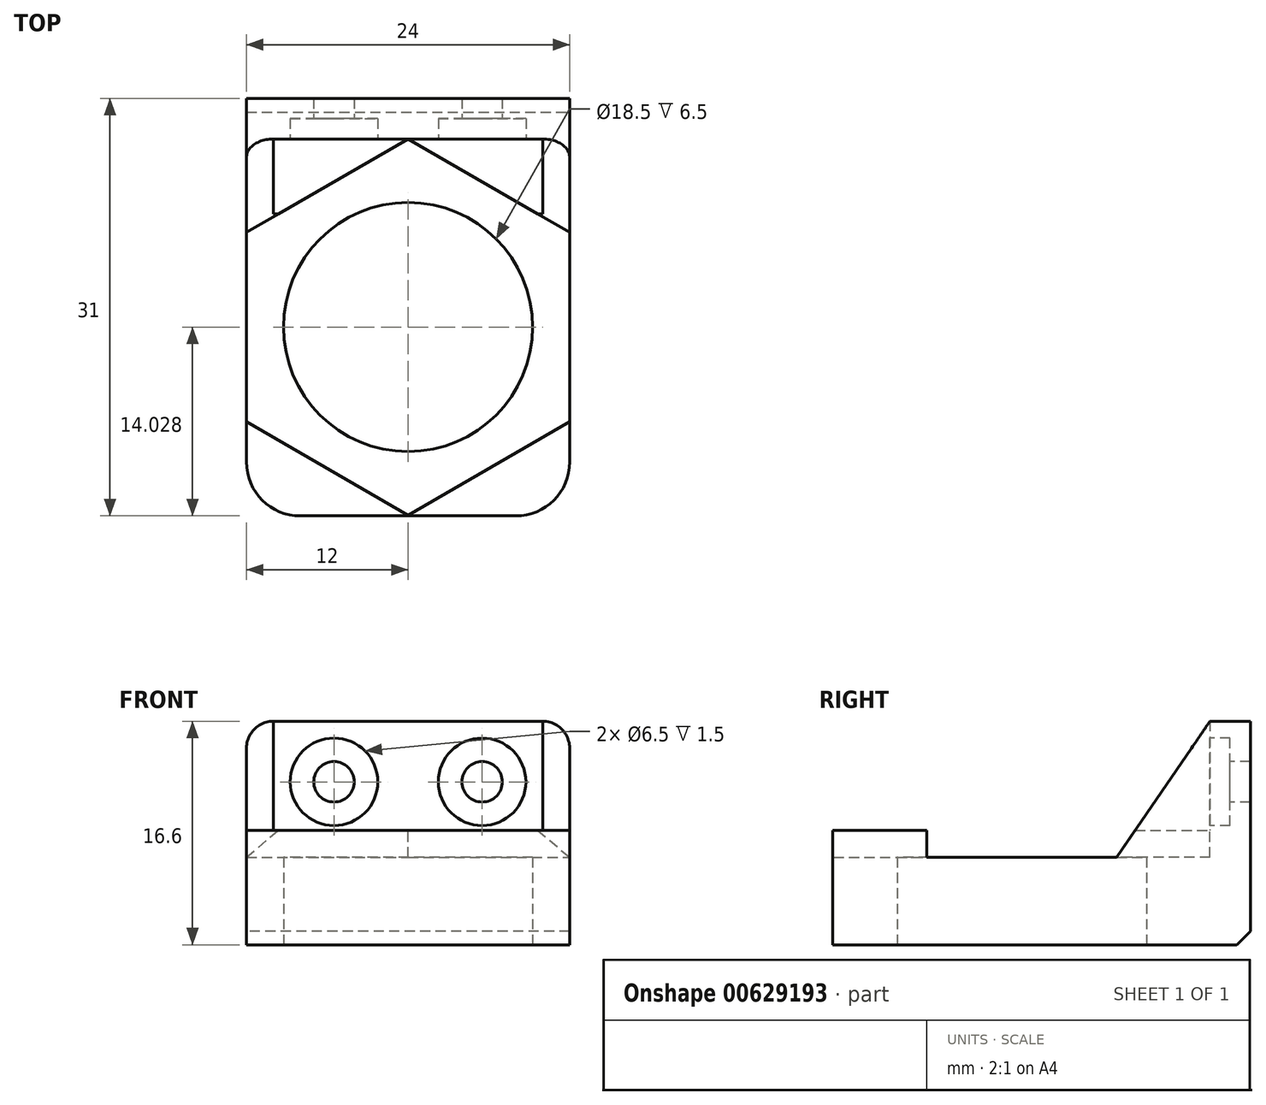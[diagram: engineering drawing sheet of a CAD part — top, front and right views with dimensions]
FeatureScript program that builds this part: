
annotation { "Feature Type Name" : "Feature", "Feature Type Description" : "" }
export const myFeature = defineFeature(function(context is Context, id is Id, definition is map)
    precondition{}
    {
        {
            var Q0;
            Q0=qCreatedBy(makeId("Front.planeOp"),FACE);
            var sketch = newSketch(context, id + "F0", { "sketchPlane" : qUnion([Q0])});
            skLineSegment(sketch, "E0.bottom", {"start": v(24, 11.6) * mm, "end": v(0, 11.6) * mm});
            skLineSegment(sketch, "E0.top", {"start": v(24, 0) * mm, "end": v(0, 0) * mm});
            skLineSegment(sketch, "E0.left", {"start": v(24, 11.6) * mm, "end": v(24, 0) * mm});
            skLineSegment(sketch, "E0.right", {"start": v(0, 11.6) * mm, "end": v(0, 0) * mm});
            skSolve(sketch);
        }
        {
            var Q0;
            Q0=makeQuery(id+"F0.imprint","IMPRINT",FACE,{"disambiguationData":[TD([[makeQuery(id+"F0.imprint","IMPRINT",EDGE,{"derivedFrom":sQuery(id+"F0.wireOp",EDGE,"E0.bottom")}),1.0]])]});
            extrude(context, id + "F1", {"entities" : qUnion([Q0]), "depth" : 3 * mm});
        }
        {
            var Q0;
            Q0=makeQuery(id+"F1.opExtrude","CAP_FACE",FACE,{"disambiguationData":[OSD([sQuery(id+"F0.wireOp",EDGE,"E0.bottom"),sQuery(id+"F0.wireOp",EDGE,"E0.top"),sQuery(id+"F0.wireOp",EDGE,"E0.left"),sQuery(id+"F0.wireOp",EDGE,"E0.right")])],"isStart":false});
            var sketch = newSketch(context, id + "F2", { "sketchPlane" : qUnion([Q0])});
            skLineSegment(sketch, "E1.bottom", {"start": v(0, 0) * mm, "end": v(24, 0) * mm});
            skLineSegment(sketch, "E1.top", {"start": v(0, 3.5) * mm, "end": v(24, 3.5) * mm});
            skLineSegment(sketch, "E1.left", {"start": v(0, 0) * mm, "end": v(0, 3.5) * mm});
            skLineSegment(sketch, "E1.right", {"start": v(24, 0) * mm, "end": v(24, 3.5) * mm});
            skLineSegment(sketch, "E2", {"start": v(0, 7.1) * mm, "end": v(24, 7.1) * mm, "construction": true});
            skLineSegment(sketch, "E3", {"start": v(17.5, 0) * mm, "end": v(17.5, 11.6) * mm, "construction": true});
            skLineSegment(sketch, "E4", {"start": v(6.5, 0) * mm, "end": v(6.5, 11.6) * mm, "construction": true});
            skPoint(sketch, "E5", {"position": v(6.5, 7.1) * mm});
            skPoint(sketch, "E6", {"position": v(17.5, 7.1) * mm});
            skCircle(sketch, "E7", {"center": v(6.5, 7.1) * mm, "radius": 2.35 * mm});
            skLineSegment(sketch, "E8", {"start": v(0, 5.8) * mm, "end": v(24, 5.8) * mm, "construction": true});
            skLineSegment(sketch, "E9", {"start": v(12, 11.6) * mm, "end": v(12, 0) * mm, "construction": true});
            skCircle(sketch, "E10.MirrorC", {"center": v(17.5, 7.1) * mm, "radius": 2.35 * mm});
            skLineSegment(sketch, "E11.bottom", {"start": v(0, 11.6) * mm, "end": v(2, 11.6) * mm});
            skLineSegment(sketch, "E11.top", {"start": v(0, 3.5) * mm, "end": v(2, 3.5) * mm});
            skLineSegment(sketch, "E11.left", {"start": v(0, 11.6) * mm, "end": v(0, 3.5) * mm});
            skLineSegment(sketch, "E11.right", {"start": v(2, 11.6) * mm, "end": v(2, 3.5) * mm});
            skLineSegment(sketch, "E12.MirrorCS", {"start": v(22, 11.6) * mm, "end": v(22, 3.5) * mm});
            skLineSegment(sketch, "E13.MirrorCS", {"start": v(24, 11.6) * mm, "end": v(22, 11.6) * mm});
            skLineSegment(sketch, "E14.MirrorCS", {"start": v(24, 11.6) * mm, "end": v(24, 3.5) * mm});
            skSolve(sketch);
        }
        {
            var Q0;
            Q0=sQuery(id+"F2.wireOp",VERTEX,"E5");
            var Q1;
            Q1=sQuery(id+"F2.wireOp",VERTEX,"E6");
            var Q2;
            Q2=sQuery(id+"F2.wireOp",VERTEX,"9b93672e-2990-476f-b0a9-77059a06add8");
            var Q3;
            Q3=sQuery(id+"F2.wireOp",VERTEX,"ac4e0633-efb0-4ba2-bce2-8fe4dab348f1");
            var Q4;
            Q4=makeQuery(id+"F1.opExtrude","SWEPT_BODY",BODY,{"disambiguationData":[OSD([sQuery(id+"F0.wireOp",EDGE,"E0.bottom"),sQuery(id+"F0.wireOp",EDGE,"E0.top"),sQuery(id+"F0.wireOp",EDGE,"E0.left"),sQuery(id+"F0.wireOp",EDGE,"E0.right")])]});
            hole(context, id + "F3", {"style" : HoleStyle.C_BORE, "endStyle" : HoleEndStyle.THROUGH, "holeDiameter" : 3 * mm, "cBoreDiameter" : 6.5 * mm, "cBoreDepth" : 1.5 * mm, "isTappedThrough" : true, "tappedDepth" : 12 * mm, "tapClearance" : 3, "locations" : qUnion([Q0, Q1, Q2, Q3]), "scope" : qUnion([Q4])});
        }
        {
            var Q0;
            Q0=makeQuery(id+"F2.imprint","IMPRINT",FACE,{"disambiguationData":[TD([[makeQuery(id+"F2.imprint","IMPRINT",EDGE,{"derivedFrom":sQuery(id+"F2.wireOp",EDGE,"E1.bottom")}),-1.0]])]});
            extrude(context, id + "F4", {"entities" : qUnion([Q0]), "operationType" : NewBodyOperationType.ADD, "depth" : 28 * mm});
        }
        {
            var Q0;
            {var subQ1=sQuery(id+"F2.wireOp",EDGE,"E1.top");Q0=makeQuery(id+"F2.imprint","IMPRINT",FACE,{"disambiguationData":[TD([[makeQuery(id+"F2.imprint","IMPRINT",EDGE,{"derivedFrom":subQ1}),1.0]])]});}
            var sketch = newSketch(context, id + "F5", { "sketchPlane" : qUnion([Q0])});
            skSolve(sketch);
        }
        {
            var Q0;
            Q0=makeQuery(id+"F4.opExtrude","SWEPT_FACE",FACE,{"disambiguationData":[OSD([sQuery(id+"F2.wireOp",EDGE,"E1.top")])]});
            var sketch = newSketch(context, id + "F6", { "sketchPlane" : qUnion([Q0])});
            skCircle(sketch, "E15.cCircle", {"center": v(12, -16.97) * mm, "radius": 12.1 * mm, "construction": true});
            skLineSegment(sketch, "E15.0", {"start": v(24.1, -9.99) * mm, "end": v(24.1, -23.96) * mm});
            skLineSegment(sketch, "E15.1", {"start": v(24.1, -23.96) * mm, "end": v(12, -30.94) * mm});
            skLineSegment(sketch, "E15.2", {"start": v(12, -30.94) * mm, "end": v(-0.1, -23.96) * mm});
            skLineSegment(sketch, "E15.3", {"start": v(-0.1, -23.96) * mm, "end": v(-0.1, -9.99) * mm});
            skLineSegment(sketch, "E15.4", {"start": v(-0.1, -9.99) * mm, "end": v(12, -3) * mm});
            skLineSegment(sketch, "E15.5", {"start": v(12, -3) * mm, "end": v(24.1, -9.99) * mm});
            skPoint(sketch, "E15.0.midPoint", {"position": v(24.1, -16.97) * mm});
            skLineSegment(sketch, "E16", {"start": v(12, -31) * mm, "end": v(12, -3) * mm, "construction": true});
            skSolve(sketch);
        }
        {
            var Q0;
            Q0=makeQuery(id+"F4.opExtrude","CAP_EDGE",EDGE,{"disambiguationData":[OSD([sQuery(id+"F2.wireOp",EDGE,"E1.right")])],"isStart":false});
            var Q1;
            Q1=makeQuery(id+"F5kRuORAZ8C9X0k_1.boolean.opBoolean","COPY",EDGE,{"derivedFrom":makeQuery(id+"F5kRuORAZ8C9X0k_1.opExtrude","SWEPT_EDGE",EDGE,{"disambiguationData":[OSD([sQuery(id+"F2.wireOp",EDGE,"E1.bottom"),sQuery(id+"F8.wireOp",EDGE,"GbdEAWLs-SJBU-rbzc-2olr-KBSKZh6psz5a")])]})});
            var Q2;
            Q2=makeQuery(id+"F5kRuORAZ8C9X0k_1.boolean.opBoolean","COPY",EDGE,{"derivedFrom":makeQuery(id+"F5kRuORAZ8C9X0k_1.opExtrude","SWEPT_EDGE",EDGE,{"disambiguationData":[OSD([sQuery(id+"F2.wireOp",EDGE,"E1.bottom"),sQuery(id+"F8.wireOp",EDGE,"kYlhJU9l-gKN5-24du-RjB6-uRuuNHYteBA4")])]})});
            var Q3;
            Q3=makeQuery(id+"F4.opExtrude","CAP_EDGE",EDGE,{"disambiguationData":[OSD([sQuery(id+"F2.wireOp",EDGE,"E1.left")])],"isStart":false});
            fillet(context, id + "F7", {"entities" : qUnion([Q0, Q1, Q2, Q3]), "radius" : 4 * mm, "tangentPropagation" : true, "allowEdgeOverflow" : false});
        }
        {
            var Q0;
            Q0=makeQuery(id+"F4.opExtrude","SWEPT_FACE",FACE,{"disambiguationData":[OSD([sQuery(id+"F2.wireOp",EDGE,"E1.bottom")])]});
            var sketch = newSketch(context, id + "F8", { "sketchPlane" : qUnion([Q0])});
            skLineSegment(sketch, "E17", {"start": v(12, 31.47) * mm, "end": v(12, 31) * mm, "construction": true});
            skCircle(sketch, "E18", {"center": v(12, 16.97) * mm, "radius": 9.25 * mm});
            skPoint(sketch, "E19", {"position": v(12, 0) * mm});
            skLineSegment(sketch, "E20", {"start": v(0, 17) * mm, "end": v(24, 17) * mm, "construction": true});
            skSolve(sketch);
        }
        {
            var Q0;
            Q0=makeQuery(id+"F8.imprint","IMPRINT",FACE,{"disambiguationData":[TD([[makeQuery(id+"F8.imprint","IMPRINT",EDGE,{"derivedFrom":sQuery(id+"F8.wireOp",EDGE,"E18")}),1.0]])]});
            extrude(context, id + "F9", {"entities" : qUnion([Q0]), "operationType" : NewBodyOperationType.REMOVE, "oppositeDirection" : true, "depth" : 25 * mm});
        }
        {
            var Q0;
            Q0=makeQuery(id+"F4.boolean.opBoolean","MERGE",FACE,{"derivedFrom":[makeQuery(id+"F1.opExtrude","SWEPT_FACE",FACE,{"disambiguationData":[OSD([sQuery(id+"F0.wireOp",EDGE,"E0.top")])]}),makeQuery(id+"F4.opExtrude","SWEPT_FACE",FACE,{"disambiguationData":[OSD([sQuery(id+"F2.wireOp",EDGE,"E1.bottom")])]})]});
            extrude(context, id + "F10", {"entities" : qUnion([Q0]), "operationType" : NewBodyOperationType.ADD, "depth" : 5 * mm});
        }
        {
            var Q0;
            {var subQ7=sQuery(id+"F6.wireOp",EDGE,"E15.2");var subQ8=sQuery(id+"F6.wireOp",EDGE,"E15.1");var subQ9=makeQuery(id+"F6.imprint","INTERSECT",VERTEX,{"derivedFrom":[subQ8,subQ7]});Q0=makeQuery(id+"F6.imprint","IMPRINT",FACE,{"disambiguationData":[TD([[makeQuery(id+"F6.imprint","IMPRINT",EDGE,{"disambiguationData":[TD([[subQ9,1.0]])],"derivedFrom":subQ8}),-1.0]])]});}
            extrude(context, id + "F11", {"entities" : qUnion([Q0]), "operationType" : NewBodyOperationType.REMOVE, "oppositeDirection" : true, "depth" : 2 * mm});
        }
        {
            var Q0;
            Q0=makeQuery(id+"F2.imprint","IMPRINT",FACE,{"disambiguationData":[TD([[makeQuery(id+"F2.imprint","IMPRINT",EDGE,{"derivedFrom":sQuery(id+"F2.wireOp",EDGE,"E11.bottom")}),1.0]])]});
            var Q1;
            Q1=makeQuery(id+"F11.boolean.opBoolean","COPY",FACE,{"derivedFrom":makeQuery(id+"F11.opExtrude","SWEPT_FACE",FACE,{"disambiguationData":[OSD([sQuery(id+"F6.wireOp",EDGE,"E15.4")])]})});
            var Q2;
            Q2=makeQuery(id+"F1.opExtrude","SWEPT_BODY",BODY,{"disambiguationData":[OSD([sQuery(id+"F0.wireOp",EDGE,"E0.bottom"),sQuery(id+"F0.wireOp",EDGE,"E0.top"),sQuery(id+"F0.wireOp",EDGE,"E0.left"),sQuery(id+"F0.wireOp",EDGE,"E0.right")])]});
            var Q3;
            Q3=sQuery(id+"F6.wireOp",VERTEX,"E15.4.start");
            extrude(context, id + "F12", {"entities" : qUnion([Q0]), "operationType" : NewBodyOperationType.ADD, "endBound" : BoundingType.UP_TO_SURFACE, "endBoundEntityFace" : qUnion([Q1]), "endBoundEntityBody" : qUnion([Q2]), "endBoundEntityVertex" : qUnion([Q3]), "depth" : 25 * mm});
        }
        {
            var Q0;
            {var subQ2=sQuery(id+"F2.wireOp",EDGE,"E12.MirrorCS");Q0=makeQuery(id+"F5.imprint","IMPRINT",FACE,{"disambiguationData":[TD([[makeQuery(id+"F5.imprint","IMPRINT",EDGE,{"derivedFrom":makeQuery(id+"F2.imprint","IMPRINT",EDGE,{"derivedFrom":subQ2})}),1.0]])]});}
            var Q1;
            Q1=makeQuery(id+"F11.boolean.opBoolean","COPY",FACE,{"derivedFrom":makeQuery(id+"F11.opExtrude","SWEPT_FACE",FACE,{"disambiguationData":[OSD([sQuery(id+"F6.wireOp",EDGE,"E15.5")])]})});
            extrude(context, id + "F13", {"entities" : qUnion([Q0]), "operationType" : NewBodyOperationType.ADD, "endBound" : BoundingType.UP_TO_SURFACE, "endBoundEntityFace" : qUnion([Q1]), "depth" : 25 * mm});
        }
        {
            var Q0;
            Q0=makeQuery(id+"F10.opExtrude","CAP_EDGE",EDGE,{"disambiguationData":[OSD([sQuery(id+"F0.wireOp",EDGE,"E0.top")])],"isStart":false});
            chamfer(context, id + "F14", {"entities" : qUnion([Q0]), "width" : 1 * mm, "tangentPropagation" : true});
        }
        {
            var Q0;
            Q0=makeQuery(id+"F1.opExtrude","SWEPT_EDGE",EDGE,{"disambiguationData":[OSD([sQuery(id+"F0.wireOp",EDGE,"E0.bottom"),sQuery(id+"F0.wireOp",EDGE,"E0.left")])]});
            var Q1;
            Q1=makeQuery(id+"F1.opExtrude","SWEPT_EDGE",EDGE,{"disambiguationData":[OSD([sQuery(id+"F0.wireOp",EDGE,"E0.bottom"),sQuery(id+"F0.wireOp",EDGE,"E0.right")])]});
            fillet(context, id + "F15", {"entities" : qUnion([Q0, Q1]), "radius" : 2 * mm, "tangentPropagation" : true, "allowEdgeOverflow" : false});
        }
        {
            var Q0;
            {var subQ0=sQuery(id+"F2.wireOp",EDGE,"E1.right");var subQ1=sQuery(id+"F0.wireOp",EDGE,"E0.left");Q0=makeQuery(id+"F13.boolean.opBoolean","MERGE",FACE,{"derivedFrom":[makeQuery(id+"F10.boolean.opBoolean","MERGE",FACE,{"derivedFrom":[makeQuery(id+"F4.boolean.opBoolean","MERGE",FACE,{"derivedFrom":[makeQuery(id+"F1.opExtrude","SWEPT_FACE",FACE,{"disambiguationData":[OSD([subQ1])]}),makeQuery(id+"F4.opExtrude","SWEPT_FACE",FACE,{"disambiguationData":[OSD([subQ0])]})]}),makeQuery(id+"F10.opExtrude","SWEPT_FACE",FACE,{"disambiguationData":[OSD([sQuery(id+"F0.wireOp",EDGE,"E0.top"),subQ1,sQuery(id+"F2.wireOp",EDGE,"E1.bottom"),subQ0])]})]}),makeQuery(id+"F13.opExtrude","SWEPT_FACE",FACE,{"disambiguationData":[OSD([sQuery(id+"F2.wireOp",EDGE,"E14.MirrorCS")])]})]});}
            var sketch = newSketch(context, id + "F16", { "sketchPlane" : qUnion([Q0])});
            skLineSegment(sketch, "E21", {"start": v(-9.93, 1.5) * mm, "end": v(-3, 11.6) * mm});
            skLineSegment(sketch, "E22", {"start": v(-3, 11.6) * mm, "end": v(-9.93, 11.6) * mm});
            skLineSegment(sketch, "E23", {"start": v(-9.93, 11.6) * mm, "end": v(-9.93, 1.5) * mm});
            skSolve(sketch);
        }
        {
            var Q0;
            Q0 = qSketchRegion(id + "F16", true);
            extrude(context, id + "F17", {"entities" : qUnion([Q0]), "operationType" : NewBodyOperationType.REMOVE, "oppositeDirection" : true, "depth" : 25 * mm, "offsetDistance" : 25 * mm});
        }
    });
